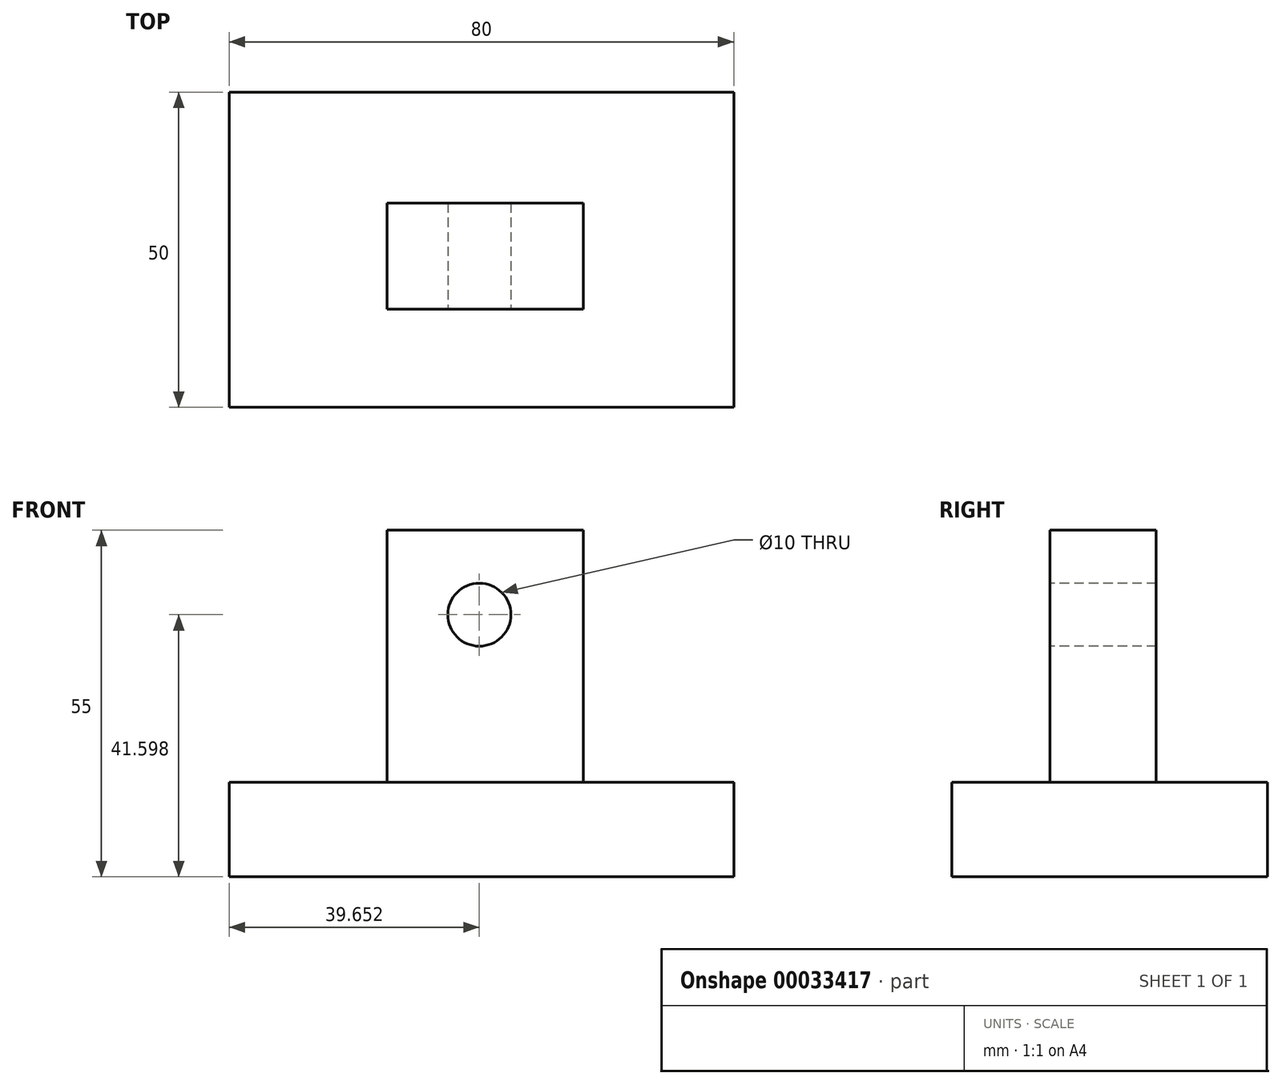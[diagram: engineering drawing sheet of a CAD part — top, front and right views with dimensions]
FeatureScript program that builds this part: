
annotation { "Feature Type Name" : "Feature", "Feature Type Description" : "" }
export const myFeature = defineFeature(function(context is Context, id is Id, definition is map)
    precondition{}
    {
        {
            var Q0;
            Q0=qCreatedBy(makeId("Top.planeOp"),FACE);
            var sketch = newSketch(context, id + "F0", { "sketchPlane" : qUnion([Q0])});
            skLineSegment(sketch, "E0.bottom", {"start": v(0, 0) * mm, "end": v(80, 0) * mm});
            skLineSegment(sketch, "E0.top", {"start": v(0, 50) * mm, "end": v(80, 50) * mm});
            skLineSegment(sketch, "E0.left", {"start": v(0, 0) * mm, "end": v(0, 50) * mm});
            skLineSegment(sketch, "E0.right", {"start": v(80, 0) * mm, "end": v(80, 50) * mm});
            skSolve(sketch);
        }
        {
            var Q0;
            Q0=makeQuery(id+"F0.imprint","IMPRINT",FACE,{"disambiguationData":[TD([[makeQuery(id+"F0.imprint","IMPRINT",EDGE,{"derivedFrom":sQuery(id+"F0.wireOp",EDGE,"E0.bottom")}),1.0]])]});
            extrude(context, id + "F1", {"entities" : qUnion([Q0]), "depth" : 15 * mm});
        }
        {
            var Q0;
            Q0=makeQuery(id+"F1.opExtrude","CAP_FACE",FACE,{"disambiguationData":[OSD([sQuery(id+"F0.wireOp",EDGE,"E0.bottom"),sQuery(id+"F0.wireOp",EDGE,"E0.top"),sQuery(id+"F0.wireOp",EDGE,"E0.left"),sQuery(id+"F0.wireOp",EDGE,"E0.right")])],"isStart":false});
            var sketch = newSketch(context, id + "F2", { "sketchPlane" : qUnion([Q0])});
            skLineSegment(sketch, "E1.bottom", {"start": v(25.05, 32.39) * mm, "end": v(56.16, 32.39) * mm});
            skLineSegment(sketch, "E1.top", {"start": v(25.05, 15.56) * mm, "end": v(56.16, 15.56) * mm});
            skLineSegment(sketch, "E1.left", {"start": v(25.05, 32.39) * mm, "end": v(25.05, 15.56) * mm});
            skLineSegment(sketch, "E1.right", {"start": v(56.16, 32.39) * mm, "end": v(56.16, 15.56) * mm});
            skSolve(sketch);
        }
        {
            var Q0;
            Q0 = qSketchRegion(id + "F2", true);
            extrude(context, id + "F3", {"entities" : qUnion([Q0]), "operationType" : NewBodyOperationType.ADD, "depth" : 40 * mm});
        }
        {
            var Q0;
            Q0=makeQuery(id+"F3.opExtrude","SWEPT_FACE",FACE,{"disambiguationData":[OSD([sQuery(id+"F2.wireOp",EDGE,"E1.top")])]});
            var sketch = newSketch(context, id + "F4", { "sketchPlane" : qUnion([Q0])});
            skCircle(sketch, "E2", {"center": v(39.65, 41.6) * mm, "radius": 5 * mm});
            skSolve(sketch);
        }
        {
            var Q0;
            Q0 = qSketchRegion(id + "F4", true);
            extrude(context, id + "F5", {"entities" : qUnion([Q0]), "operationType" : NewBodyOperationType.REMOVE, "endBound" : BoundingType.THROUGH_ALL, "oppositeDirection" : true, "depth" : 25 * mm});
        }
    });
